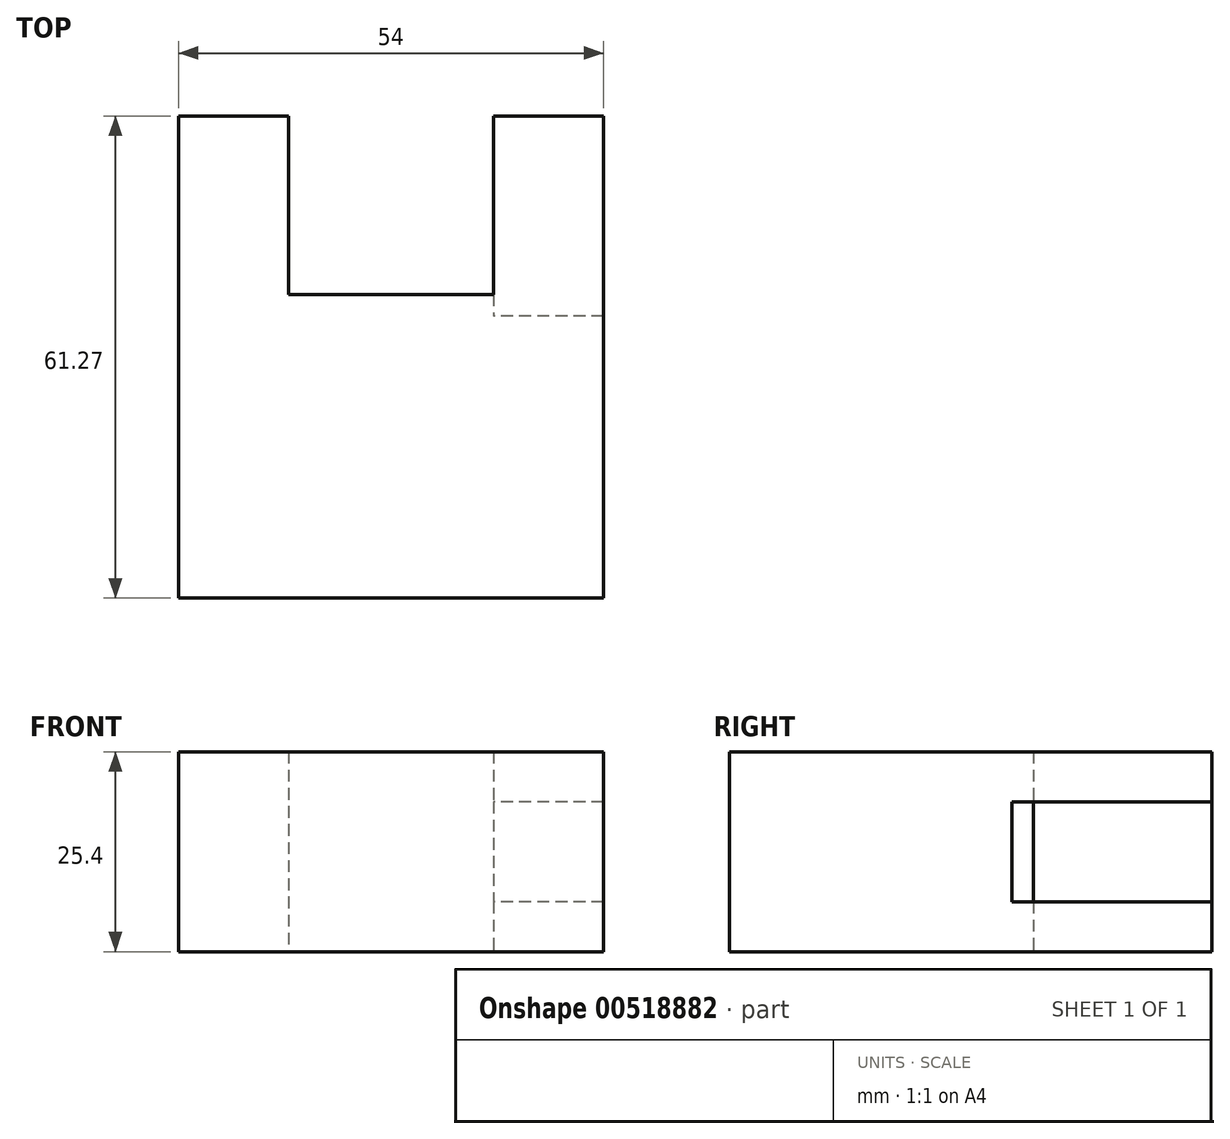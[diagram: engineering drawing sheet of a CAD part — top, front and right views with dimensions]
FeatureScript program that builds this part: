
annotation { "Feature Type Name" : "Feature", "Feature Type Description" : "" }
export const myFeature = defineFeature(function(context is Context, id is Id, definition is map)
    precondition{}
    {
        {
            var Q0;
            Q0=qCreatedBy(makeId("Top.planeOp"),FACE);
            var sketch = newSketch(context, id + "F0", { "sketchPlane" : qUnion([Q0])});
            skLineSegment(sketch, "E0.bottom", {"start": v(0, 0) * mm, "end": v(54, 0) * mm});
            skLineSegment(sketch, "E0.top", {"start": v(0, 35.87) * mm, "end": v(14, 35.87) * mm});
            skLineSegment(sketch, "E0.left", {"start": v(0, 0) * mm, "end": v(0, 35.87) * mm});
            skLineSegment(sketch, "E0.right", {"start": v(54, 0) * mm, "end": v(54, 35.87) * mm});
            skLineSegment(sketch, "E1.top", {"start": v(14, 13.2) * mm, "end": v(40, 13.2) * mm});
            skLineSegment(sketch, "E1.left", {"start": v(14, 35.87) * mm, "end": v(14, 13.2) * mm});
            skLineSegment(sketch, "E1.right", {"start": v(40, 35.87) * mm, "end": v(40, 13.2) * mm});
            skLineSegment(sketch, "E2.trimOffspring", {"start": v(40, 35.87) * mm, "end": v(54, 35.87) * mm});
            skSolve(sketch);
        }
        {
            var Q0;
            Q0 = qSketchRegion(id + "F0", true);
            extrude(context, id + "F1", {"entities" : qUnion([Q0]), "depth" : 25.4 * mm});
        }
        {
            var Q0;
            Q0=makeQuery(id+"F1.opExtrude","SWEPT_FACE",FACE,{"disambiguationData":[OSD([sQuery(id+"F0.wireOp",EDGE,"E2.trimOffspring")])]});
            var sketch = newSketch(context, id + "F2", { "sketchPlane" : qUnion([Q0])});
            skLineSegment(sketch, "E3", {"start": v(-54, 6.35) * mm, "end": v(-40, 6.35) * mm});
            skLineSegment(sketch, "E4", {"start": v(-40, 6.35) * mm, "end": v(-40, 12.7) * mm});
            skLineSegment(sketch, "E5", {"start": v(-54, 25.4) * mm, "end": v(-54, 12.7) * mm});
            skLineSegment(sketch, "E6.MirrorCS", {"start": v(-54, 12.7) * mm, "end": v(-40, 12.7) * mm});
            skLineSegment(sketch, "E7.MirrorCS", {"start": v(-54, 0) * mm, "end": v(-40, 0) * mm});
            skLineSegment(sketch, "E8.MirrorCS", {"start": v(-54, 19.05) * mm, "end": v(-40, 19.05) * mm});
            skSolve(sketch);
        }
        {
            var Q0;
            {var subQ0=sQuery(id+"F2.wireOp",EDGE,"E3");Q0=makeQuery(id+"F2.imprint","IMPRINT",FACE,{"disambiguationData":[TD([[makeQuery(id+"F2.imprint","IMPRINT",EDGE,{"derivedFrom":subQ0}),-1.0]])]});}
            var Q1;
            Q1=makeQuery(id+"F1.opExtrude","SWEPT_FACE",FACE,{"disambiguationData":[OSD([sQuery(id+"F0.wireOp",EDGE,"E1.top")])]});
            var Q2;
            {var subQ3=sQuery(id+"F2.wireOp",EDGE,"E8.MirrorCS");Q2=makeQuery(id+"F2.imprint","IMPRINT",FACE,{"disambiguationData":[TD([[makeQuery(id+"F2.imprint","IMPRINT",EDGE,{"derivedFrom":subQ3}),1.0]])]});}
            var Q3;
            Q3=makeQuery(id+"F1.opExtrude","SWEPT_FACE",FACE,{"disambiguationData":[OSD([sQuery(id+"F0.wireOp",EDGE,"E0.top")])]});
            extrude(context, id + "F3", {"entities" : qUnion([Q0, Q1, Q2, Q3]), "operationType" : NewBodyOperationType.ADD, "depth" : 25.4 * mm});
        }
    });
